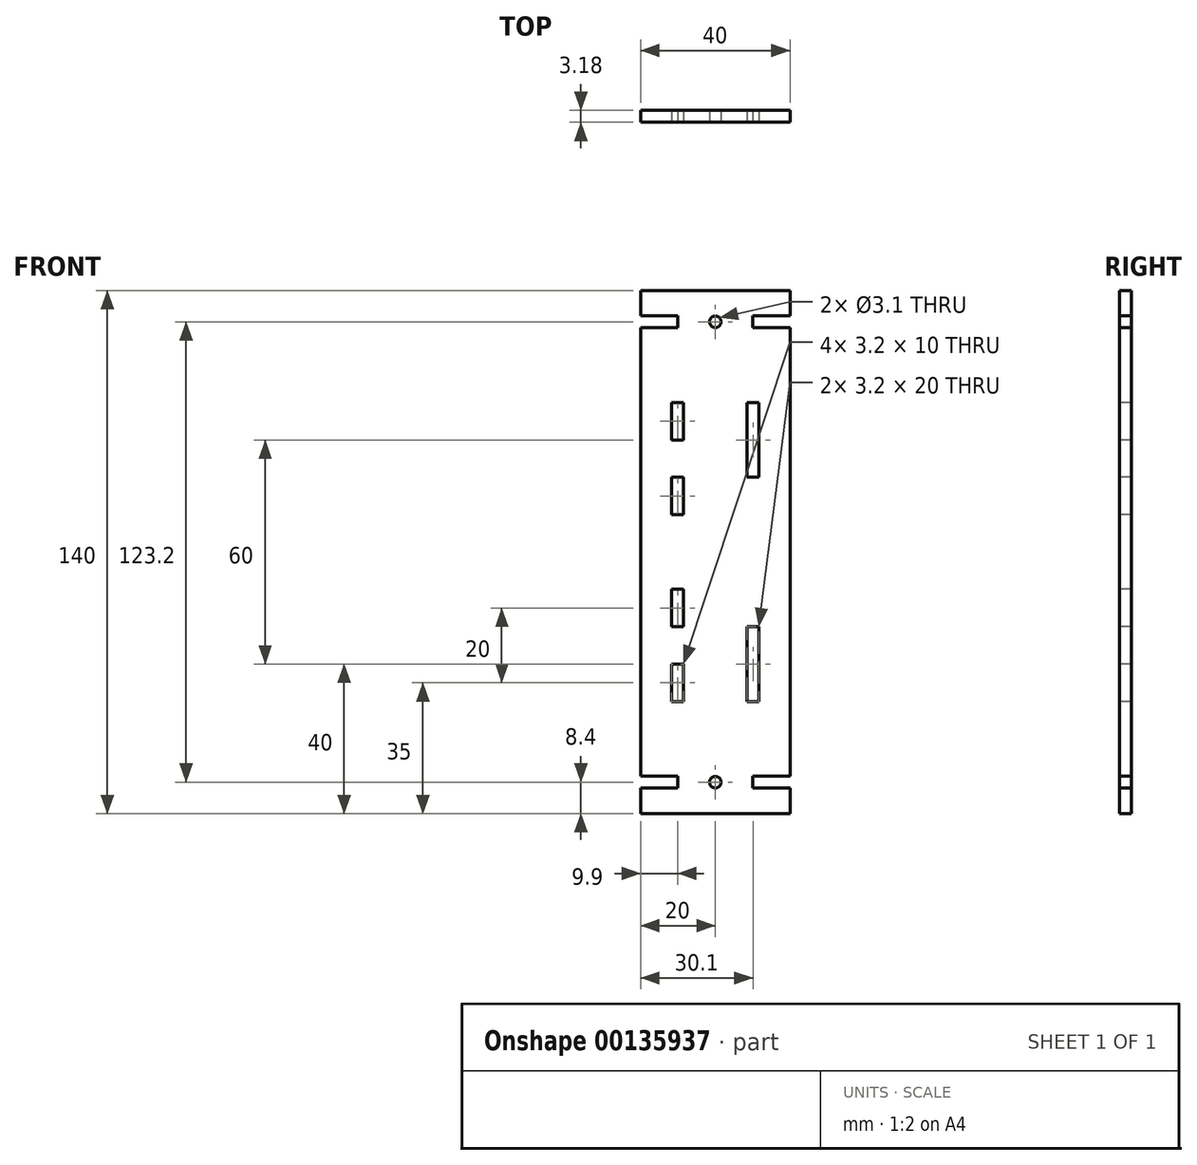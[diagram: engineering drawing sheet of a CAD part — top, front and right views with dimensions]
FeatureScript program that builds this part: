
annotation { "Feature Type Name" : "Feature", "Feature Type Description" : "" }
export const myFeature = defineFeature(function(context is Context, id is Id, definition is map)
    precondition{}
    {
        {
            var Q0;
            Q0=qCreatedBy(makeId("Front.planeOp"),FACE);
            var sketch = newSketch(context, id + "F0", { "sketchPlane" : qUnion([Q0])});
            skLineSegment(sketch, "E0", {"start": v(20, 0) * mm, "end": v(20, 60) * mm});
            skLineSegment(sketch, "E1", {"start": v(20, 60) * mm, "end": v(10, 60) * mm});
            skLineSegment(sketch, "E2", {"start": v(10, 60) * mm, "end": v(10, 63.2) * mm});
            skLineSegment(sketch, "E3", {"start": v(10, 63.2) * mm, "end": v(20, 63.2) * mm});
            skLineSegment(sketch, "E4", {"start": v(20, 63.2) * mm, "end": v(20, 70) * mm});
            skLineSegment(sketch, "E5", {"start": v(20, 70) * mm, "end": v(0, 70) * mm});
            skLineSegment(sketch, "E6.MirrorCS", {"start": v(-10, 60) * mm, "end": v(-10, 63.2) * mm});
            skLineSegment(sketch, "E7.MirrorCS", {"start": v(-20, 70) * mm, "end": v(0, 70) * mm});
            skLineSegment(sketch, "E8.MirrorCS", {"start": v(-20, 0) * mm, "end": v(-20, 60) * mm});
            skLineSegment(sketch, "E9.MirrorCS", {"start": v(-20, 63.2) * mm, "end": v(-20, 70) * mm});
            skLineSegment(sketch, "E10.MirrorCS", {"start": v(-20, 60) * mm, "end": v(-10, 60) * mm});
            skLineSegment(sketch, "E11.MirrorCS", {"start": v(-10, 63.2) * mm, "end": v(-20, 63.2) * mm});
            skLineSegment(sketch, "E12.MirrorCS", {"start": v(-10, -60) * mm, "end": v(-10, -63.2) * mm});
            skLineSegment(sketch, "E13.MirrorCS", {"start": v(10, -60) * mm, "end": v(10, -63.2) * mm});
            skLineSegment(sketch, "E14.MirrorCS", {"start": v(-10, -63.2) * mm, "end": v(-20, -63.2) * mm});
            skLineSegment(sketch, "E15.MirrorCS", {"start": v(-20, -60) * mm, "end": v(-10, -60) * mm});
            skLineSegment(sketch, "E16.MirrorCS", {"start": v(-20, -63.2) * mm, "end": v(-20, -70) * mm});
            skLineSegment(sketch, "E17.MirrorCS", {"start": v(-20, 0) * mm, "end": v(-20, -60) * mm});
            skLineSegment(sketch, "E18.MirrorCS", {"start": v(-20, -70) * mm, "end": v(0, -70) * mm});
            skLineSegment(sketch, "E19.MirrorCS", {"start": v(20, -70) * mm, "end": v(0, -70) * mm});
            skLineSegment(sketch, "E20.MirrorCS", {"start": v(10, -63.2) * mm, "end": v(20, -63.2) * mm});
            skLineSegment(sketch, "E21.MirrorCS", {"start": v(20, 0) * mm, "end": v(20, -60) * mm});
            skLineSegment(sketch, "E22.MirrorCS", {"start": v(20, -63.2) * mm, "end": v(20, -70) * mm});
            skLineSegment(sketch, "E23.MirrorCS", {"start": v(20, -60) * mm, "end": v(10, -60) * mm});
            skPoint(sketch, "E24", {"position": v(10, 61.6) * mm});
            skCircle(sketch, "E25", {"center": v(0, 61.6) * mm, "radius": 1.55 * mm});
            skCircle(sketch, "E26.MirrorC", {"center": v(0, -61.6) * mm, "radius": 1.55 * mm});
            skLineSegment(sketch, "E27.bottom", {"start": v(11.7, 10) * mm, "end": v(8.5, 10) * mm});
            skLineSegment(sketch, "E27.top", {"start": v(11.7, 20) * mm, "end": v(8.5, 20) * mm});
            skLineSegment(sketch, "E27.left", {"start": v(11.7, 10) * mm, "end": v(11.7, 20) * mm});
            skLineSegment(sketch, "E27.right", {"start": v(8.5, 10) * mm, "end": v(8.5, 20) * mm});
            skLineSegment(sketch, "E28.bottom", {"start": v(8.5, 30) * mm, "end": v(11.7, 30) * mm});
            skLineSegment(sketch, "E28.top", {"start": v(8.5, 40) * mm, "end": v(11.7, 40) * mm});
            skLineSegment(sketch, "E28.left", {"start": v(8.5, 30) * mm, "end": v(8.5, 40) * mm});
            skLineSegment(sketch, "E28.right", {"start": v(11.7, 30) * mm, "end": v(11.7, 40) * mm});
            skLineSegment(sketch, "E29.bottom", {"start": v(-8.5, 40) * mm, "end": v(-11.7, 40) * mm});
            skLineSegment(sketch, "E29.top", {"start": v(-8.5, 20) * mm, "end": v(-11.7, 20) * mm});
            skLineSegment(sketch, "E29.left", {"start": v(-8.5, 40) * mm, "end": v(-8.5, 20) * mm});
            skLineSegment(sketch, "E29.right", {"start": v(-11.7, 40) * mm, "end": v(-11.7, 20) * mm});
            skLineSegment(sketch, "E30.MirrorCS", {"start": v(-8.5, -40) * mm, "end": v(-11.7, -40) * mm});
            skLineSegment(sketch, "E31.MirrorCS", {"start": v(8.5, -40) * mm, "end": v(11.7, -40) * mm});
            skLineSegment(sketch, "E32.MirrorCS", {"start": v(11.7, -10) * mm, "end": v(8.5, -10) * mm});
            skLineSegment(sketch, "E33.MirrorCS", {"start": v(-8.5, -20) * mm, "end": v(-11.7, -20) * mm});
            skLineSegment(sketch, "E34.MirrorCS", {"start": v(8.5, -30) * mm, "end": v(11.7, -30) * mm});
            skLineSegment(sketch, "E35.MirrorCS", {"start": v(11.7, -20) * mm, "end": v(8.5, -20) * mm});
            skLineSegment(sketch, "E36.MirrorCS", {"start": v(8.5, -30) * mm, "end": v(8.5, -40) * mm});
            skLineSegment(sketch, "E37.MirrorCS", {"start": v(8.5, -10) * mm, "end": v(8.5, -20) * mm});
            skLineSegment(sketch, "E38.MirrorCS", {"start": v(-8.5, -40) * mm, "end": v(-8.5, -20) * mm});
            skLineSegment(sketch, "E39.MirrorCS", {"start": v(11.7, -10) * mm, "end": v(11.7, -20) * mm});
            skLineSegment(sketch, "E40.MirrorCS", {"start": v(11.7, -30) * mm, "end": v(11.7, -40) * mm});
            skLineSegment(sketch, "E41.MirrorCS", {"start": v(-11.7, -40) * mm, "end": v(-11.7, -20) * mm});
            skSolve(sketch);
        }
        {
            var Q0;
            Q0=makeQuery(id+"F0.imprint","IMPRINT",FACE,{"disambiguationData":[TD([[makeQuery(id+"F0.imprint","IMPRINT",EDGE,{"derivedFrom":sQuery(id+"F0.wireOp",EDGE,"E0")}),1.0]])]});
            extrude(context, id + "F1", {"entities" : qUnion([Q0]), "depth" : 3.17 * mm, "symmetric" : true});
        }
        {
            var Q0;
            Q0=qCreatedBy(makeId("Front.planeOp"),FACE);
            var sketch = newSketch(context, id + "F2", { "sketchPlane" : qUnion([Q0])});
            skLineSegment(sketch, "E42", {"start": v(0, 63.22) * mm, "end": v(0, -77.18) * mm});
            skSolve(sketch);
        }
        {
            var Q0;
            Q0=makeQuery(id+"F1.opExtrude","SWEPT_BODY",BODY,{"disambiguationData":[OSD([sQuery(id+"F0.wireOp",EDGE,"E0"),sQuery(id+"F0.wireOp",EDGE,"E1"),sQuery(id+"F0.wireOp",EDGE,"E2"),sQuery(id+"F0.wireOp",EDGE,"E3"),sQuery(id+"F0.wireOp",EDGE,"E4"),sQuery(id+"F0.wireOp",EDGE,"E5"),sQuery(id+"F0.wireOp",EDGE,"E6.MirrorCS"),sQuery(id+"F0.wireOp",EDGE,"E7.MirrorCS"),sQuery(id+"F0.wireOp",EDGE,"E8.MirrorCS"),sQuery(id+"F0.wireOp",EDGE,"E9.MirrorCS"),sQuery(id+"F0.wireOp",EDGE,"E10.MirrorCS"),sQuery(id+"F0.wireOp",EDGE,"E11.MirrorCS"),sQuery(id+"F0.wireOp",EDGE,"E12.MirrorCS"),sQuery(id+"F0.wireOp",EDGE,"E13.MirrorCS"),sQuery(id+"F0.wireOp",EDGE,"E14.MirrorCS"),sQuery(id+"F0.wireOp",EDGE,"E15.MirrorCS"),sQuery(id+"F0.wireOp",EDGE,"E16.MirrorCS"),sQuery(id+"F0.wireOp",EDGE,"E17.MirrorCS"),sQuery(id+"F0.wireOp",EDGE,"E18.MirrorCS"),sQuery(id+"F0.wireOp",EDGE,"E19.MirrorCS"),sQuery(id+"F0.wireOp",EDGE,"E20.MirrorCS"),sQuery(id+"F0.wireOp",EDGE,"E21.MirrorCS"),sQuery(id+"F0.wireOp",EDGE,"E22.MirrorCS"),sQuery(id+"F0.wireOp",EDGE,"E23.MirrorCS"),sQuery(id+"F0.wireOp",EDGE,"E25"),sQuery(id+"F0.wireOp",EDGE,"E26.MirrorC"),sQuery(id+"F0.wireOp",EDGE,"E27.bottom"),sQuery(id+"F0.wireOp",EDGE,"E27.top"),sQuery(id+"F0.wireOp",EDGE,"E27.left"),sQuery(id+"F0.wireOp",EDGE,"E27.right"),sQuery(id+"F0.wireOp",EDGE,"E28.bottom"),sQuery(id+"F0.wireOp",EDGE,"E28.top"),sQuery(id+"F0.wireOp",EDGE,"E28.left"),sQuery(id+"F0.wireOp",EDGE,"E28.right"),sQuery(id+"F0.wireOp",EDGE,"E29.bottom"),sQuery(id+"F0.wireOp",EDGE,"E29.top"),sQuery(id+"F0.wireOp",EDGE,"E29.left"),sQuery(id+"F0.wireOp",EDGE,"E29.right"),sQuery(id+"F0.wireOp",EDGE,"E30.MirrorCS"),sQuery(id+"F0.wireOp",EDGE,"E31.MirrorCS"),sQuery(id+"F0.wireOp",EDGE,"E32.MirrorCS"),sQuery(id+"F0.wireOp",EDGE,"E33.MirrorCS"),sQuery(id+"F0.wireOp",EDGE,"E34.MirrorCS"),sQuery(id+"F0.wireOp",EDGE,"E35.MirrorCS"),sQuery(id+"F0.wireOp",EDGE,"E36.MirrorCS"),sQuery(id+"F0.wireOp",EDGE,"E37.MirrorCS"),sQuery(id+"F0.wireOp",EDGE,"E38.MirrorCS"),sQuery(id+"F0.wireOp",EDGE,"E39.MirrorCS"),sQuery(id+"F0.wireOp",EDGE,"E40.MirrorCS"),sQuery(id+"F0.wireOp",EDGE,"E41.MirrorCS")])]});
            var Q1;
            Q1=sQuery(id+"F2.wireOp",EDGE,"E42");
            transform(context, id + "F3", {"entities" : qUnion([Q0]), "transformType" : TransformType.ROTATION, "transformAxis" : qUnion([Q1]), "angle" : 180 * degree, "makeCopy" : false});
        }
    });
